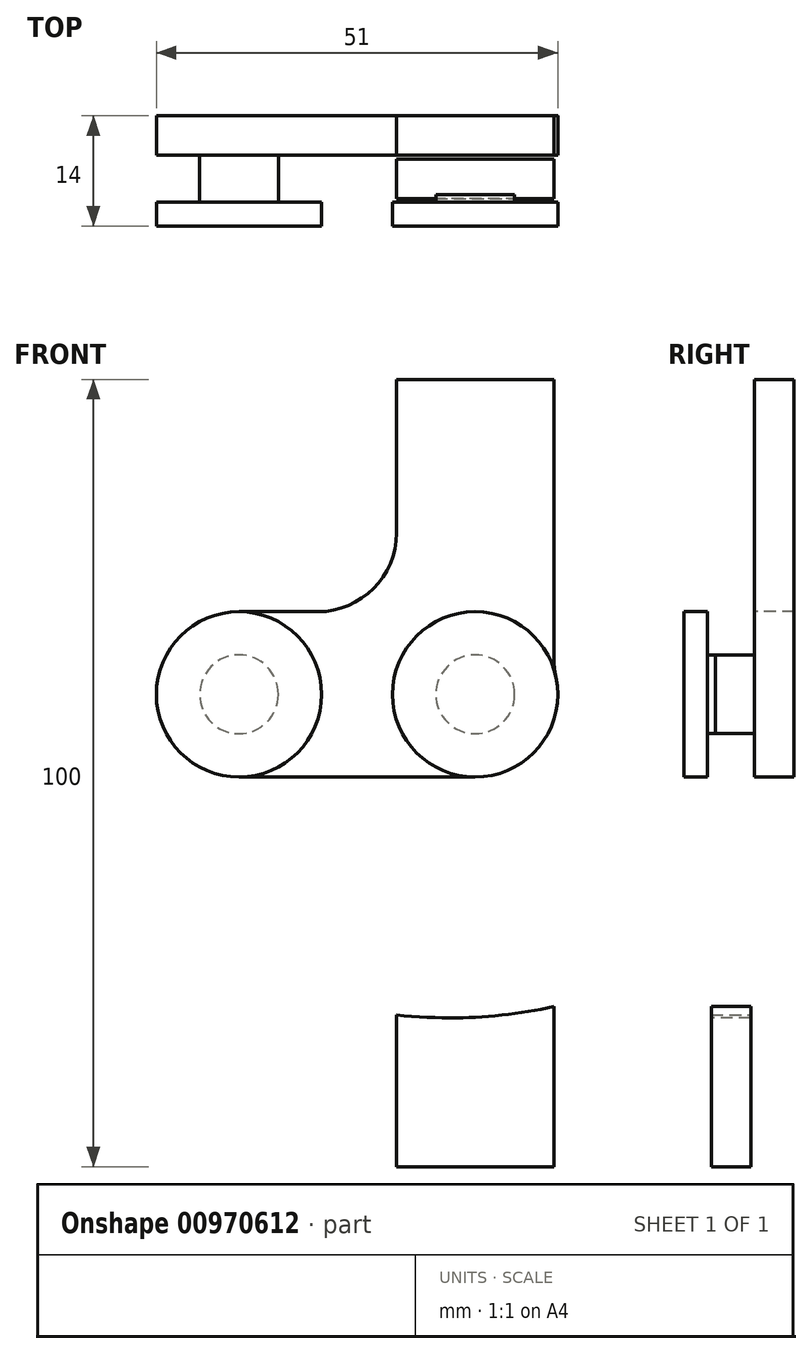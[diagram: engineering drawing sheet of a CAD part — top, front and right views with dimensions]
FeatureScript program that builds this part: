
annotation { "Feature Type Name" : "Feature", "Feature Type Description" : "" }
export const myFeature = defineFeature(function(context is Context, id is Id, definition is map)
    precondition{}
    {
        {
            assignVariable(context, id + "F0", {"name" : "Tbrace", "anyValue" : 5});
        }
        {
            assignVariable(context, id + "F1", {"name" : "Zclearance", "anyValue" : 0.5});
        }
        {
            assignVariable(context, id + "F2", {"name" : "Hpin", "anyValue" : getVariable(context, 'Tbrace') + 2 * getVariable(context, 'Zclearance')});
        }
        {
            assignVariable(context, id + "F3", {"name" : "Tcap", "anyValue" : 3});
        }
        {
            var Q0;
            Q0=qCreatedBy(makeId("Front.planeOp"),FACE);
            var sketch = newSketch(context, id + "F4", { "sketchPlane" : qUnion([Q0])});
            skCircle(sketch, "E0", {"center": v(0, 0) * mm, "radius": 5 * mm});
            skCircle(sketch, "E1", {"center": v(-30, 0) * mm, "radius": 5 * mm});
            skLineSegment(sketch, "E2", {"start": v(0, 0) * mm, "end": v(-30, 0) * mm, "construction": true});
            skSolve(sketch);
        }
        {
            var Q0;
            Q0=qCreatedBy(makeId("Front.planeOp"),FACE);
            var sketch = newSketch(context, id + "F5", { "sketchPlane" : qUnion([Q0])});
            skArc(sketch, "E3", {"start": v(0, 0) * mm, "mid": v(4.76, 8.78) * mm, "end": v(7.87, 18.27) * mm, "construction": true});
            skLineSegment(sketch, "E4", {"start": v(-46.2, 30.74) * mm, "end": v(0, 0) * mm, "construction": true});
            skLineSegment(sketch, "E5", {"start": v(-46.2, 30.74) * mm, "end": v(7.87, 18.27) * mm, "construction": true});
            skArc(sketch, "E6.0.startCap", {"start": v(4.58, -3.05) * mm, "mid": v(-3.05, -4.58) * mm, "end": v(-4.58, 3.05) * mm});
            skArc(sketch, "E6.0.endCap", {"start": v(2.51, 19.5) * mm, "mid": v(9.11, 23.63) * mm, "end": v(13.23, 17.03) * mm});
            skArc(sketch, "E6.0.left", {"start": v(-4.58, 3.05) * mm, "mid": v(-0.29, 10.96) * mm, "end": v(2.51, 19.5) * mm});
            skArc(sketch, "E6.0.right", {"start": v(4.58, -3.05) * mm, "mid": v(9.81, 6.6) * mm, "end": v(13.23, 17.03) * mm});
            skPoint(sketch, "E7", {"position": v(25.08, -6.3) * mm});
            skLineSegment(sketch, "E8", {"start": v(7.87, 18.27) * mm, "end": v(25.08, -6.3) * mm, "construction": true});
            skLineSegment(sketch, "E9.1.0", {"start": v(-46.2, 30.74) * mm, "end": v(1.08, 1.68) * mm, "construction": true});
            skLineSegment(sketch, "E9.2.0", {"start": v(-46.2, 30.74) * mm, "end": v(2.1, 3.4) * mm, "construction": true});
            skLineSegment(sketch, "E9.3.0", {"start": v(-46.2, 30.74) * mm, "end": v(3.05, 5.17) * mm, "construction": true});
            skLineSegment(sketch, "E9.4.0", {"start": v(-46.2, 30.74) * mm, "end": v(3.94, 6.96) * mm, "construction": true});
            skLineSegment(sketch, "E9.5.0", {"start": v(-46.2, 30.74) * mm, "end": v(4.76, 8.78) * mm, "construction": true});
            skLineSegment(sketch, "E9.6.0", {"start": v(-46.2, 30.74) * mm, "end": v(5.52, 10.63) * mm, "construction": true});
            skLineSegment(sketch, "E9.7.0", {"start": v(-46.2, 30.74) * mm, "end": v(6.21, 12.5) * mm, "construction": true});
            skLineSegment(sketch, "E9.8.0", {"start": v(-46.2, 30.74) * mm, "end": v(6.84, 14.4) * mm, "construction": true});
            skLineSegment(sketch, "E9.9.0", {"start": v(-46.2, 30.74) * mm, "end": v(7.39, 16.33) * mm, "construction": true});
            skLineSegment(sketch, "E10", {"start": v(7.39, 16.33) * mm, "end": v(18.87, -11.39) * mm, "construction": true});
            skLineSegment(sketch, "E11", {"start": v(6.84, 14.4) * mm, "end": v(12.04, -15.14) * mm, "construction": true});
            skLineSegment(sketch, "E12", {"start": v(6.21, 12.5) * mm, "end": v(4.9, -17.47) * mm, "construction": true});
            skLineSegment(sketch, "E13", {"start": v(5.52, 10.63) * mm, "end": v(-2.24, -18.35) * mm, "construction": true});
            skLineSegment(sketch, "E14", {"start": v(4.76, 8.78) * mm, "end": v(-9.1, -17.83) * mm, "construction": true});
            skLineSegment(sketch, "E15", {"start": v(3.94, 6.96) * mm, "end": v(-15.35, -16.02) * mm, "construction": true});
            skLineSegment(sketch, "E16", {"start": v(3.05, 5.17) * mm, "end": v(-20.75, -13.1) * mm, "construction": true});
            skLineSegment(sketch, "E17", {"start": v(2.1, 3.4) * mm, "end": v(-25.1, -9.27) * mm, "construction": true});
            skLineSegment(sketch, "E18", {"start": v(1.08, 1.68) * mm, "end": v(-28.21, -4.8) * mm, "construction": true});
            skLineSegment(sketch, "E19", {"start": v(0, 0) * mm, "end": v(-30, 0) * mm, "construction": true});
            skFitSpline(sketch, "E20", {"points": [v(-30, 0) * mm, v(-28.21, -4.8) * mm, v(-25.1, -9.27) * mm, v(-20.75, -13.1) * mm, v(-15.35, -16.02) * mm, v(-9.1, -17.83) * mm, v(-2.24, -18.35) * mm, v(4.9, -17.47) * mm, v(12.04, -15.14) * mm, v(18.87, -11.39) * mm, v(25.08, -6.3) * mm], "startDerivative": vector(0, -79.8) * mm, "endDerivative": vector(58.42, 58.42) * mm, "construction": true});
            skLineSegment(sketch, "E21.0.startCap", {"start": v(-35.5, 0) * mm, "end": v(-35.5, 0) * mm});
            skLineSegment(sketch, "E21.0.endCap", {"start": v(28.97, -10.2) * mm, "end": v(28.97, -10.2) * mm});
            skFitSpline(sketch, "E21.0.left", {"points": [v(-48, 0) * mm, v(-48, -0.78) * mm, v(-47.9, -2.28) * mm, v(-47.5, -4.33) * mm, v(-46.97, -6.18) * mm, v(-46.46, -7.56) * mm, v(-46.03, -8.58) * mm, v(-45.71, -9.3) * mm, v(-45.45, -9.88) * mm, v(-45.24, -10.32) * mm, v(-45.04, -10.74) * mm, v(-44.78, -11.28) * mm, v(-44.34, -12.15) * mm, v(-43.77, -13.24) * mm, v(-43.02, -14.57) * mm, v(-42.22, -15.9) * mm, v(-41.49, -17) * mm, v(-40.86, -17.88) * mm, v(-40.21, -18.76) * mm, v(-39.37, -19.83) * mm, v(-38.3, -21.06) * mm, v(-37.19, -22.25) * mm, v(-35.65, -23.76) * mm, v(-33.63, -25.52) * mm, v(-30.22, -28.1) * mm, v(-26.52, -30.33) * mm, v(-22.58, -32.16) * mm, v(-18.53, -33.72) * mm, v(-13.25, -35.16) * mm, v(-6.74, -36.05) * mm, v(-1.22, -36.1) * mm, v(3.19, -35.74) * mm, v(7.6, -35.1) * mm, v(11.94, -34.06) * mm, v(16.16, -32.67) * mm, v(19.25, -31.44) * mm, v(22.28, -30.04) * mm, v(24.76, -28.7) * mm, v(26.73, -27.55) * mm, v(28.69, -26.32) * mm, v(31.12, -24.67) * mm, v(33.92, -22.52) * mm, v(35.65, -20.98) * mm, v(36.47, -20.15) * mm]});
            skFitSpline(sketch, "E21.0.right", {"points": [v(-48, 0) * mm, v(-48, -0.78) * mm, v(-47.9, -2.28) * mm, v(-47.5, -4.33) * mm, v(-46.97, -6.18) * mm, v(-46.46, -7.56) * mm, v(-46.03, -8.58) * mm, v(-45.71, -9.3) * mm, v(-45.45, -9.88) * mm, v(-45.24, -10.32) * mm, v(-45.04, -10.74) * mm, v(-44.78, -11.28) * mm, v(-44.34, -12.15) * mm, v(-43.77, -13.24) * mm, v(-43.02, -14.57) * mm, v(-42.22, -15.9) * mm, v(-41.49, -17) * mm, v(-40.86, -17.88) * mm, v(-40.21, -18.76) * mm, v(-39.37, -19.83) * mm, v(-38.3, -21.06) * mm, v(-37.19, -22.25) * mm, v(-35.65, -23.76) * mm, v(-33.63, -25.52) * mm, v(-30.22, -28.1) * mm, v(-26.52, -30.33) * mm, v(-22.58, -32.16) * mm, v(-18.53, -33.72) * mm, v(-13.25, -35.16) * mm, v(-6.74, -36.05) * mm, v(-1.22, -36.1) * mm, v(3.19, -35.74) * mm, v(7.6, -35.1) * mm, v(11.94, -34.06) * mm, v(16.16, -32.67) * mm, v(19.25, -31.44) * mm, v(22.28, -30.04) * mm, v(24.76, -28.7) * mm, v(26.73, -27.55) * mm, v(28.69, -26.32) * mm, v(31.12, -24.67) * mm, v(33.92, -22.52) * mm, v(35.65, -20.98) * mm, v(36.47, -20.15) * mm]});
            skFitSpline(sketch, "E22.0", {"points": [v(-32, 0) * mm, v(-32, -0.05) * mm, v(-32, -0.17) * mm, v(-31.96, -0.4) * mm, v(-31.92, -0.6) * mm, v(-31.85, -0.86) * mm, v(-31.76, -1.16) * mm, v(-31.64, -1.5) * mm, v(-31.5, -1.86) * mm, v(-31.33, -2.27) * mm, v(-31.14, -2.7) * mm, v(-30.92, -3.18) * mm, v(-30.68, -3.69) * mm, v(-30.43, -4.19) * mm, v(-30.1, -4.83) * mm, v(-29.7, -5.62) * mm, v(-29.2, -6.5) * mm, v(-28.69, -7.35) * mm, v(-28.16, -8.14) * mm, v(-27.63, -8.89) * mm, v(-27.05, -9.61) * mm, v(-26.42, -10.34) * mm, v(-25.75, -11.05) * mm, v(-25.04, -11.75) * mm, v(-24.3, -12.43) * mm, v(-23.51, -13.1) * mm, v(-22.7, -13.73) * mm, v(-21.58, -14.54) * mm, v(-20.41, -15.3) * mm, v(-19.2, -16) * mm, v(-17.95, -16.67) * mm, v(-16.33, -17.42) * mm, v(-13.64, -18.46) * mm, v(-10.78, -19.24) * mm, v(-7.83, -19.74) * mm, v(-4.8, -20.06) * mm, v(-1.72, -20.09) * mm, v(1.38, -19.83) * mm, v(3.72, -19.5) * mm, v(6.07, -19) * mm, v(8.4, -18.38) * mm, v(10.7, -17.62) * mm, v(12.92, -16.74) * mm, v(14.75, -15.9) * mm, v(16.2, -15.13) * mm, v(17.31, -14.52) * mm, v(18.43, -13.87) * mm, v(19.56, -13.16) * mm, v(20.67, -12.43) * mm, v(21.75, -11.67) * mm, v(22.6, -11.04) * mm, v(23.23, -10.55) * mm, v(23.68, -10.18) * mm, v(24.1, -9.82) * mm, v(24.62, -9.36) * mm, v(24.96, -9.04) * mm, v(25.16, -8.84) * mm]});
            skArc(sketch, "E23", {"start": v(-35.5, 0) * mm, "mid": v(-30, 5.5) * mm, "end": v(-24.5, 0) * mm});
            skArc(sketch, "E24", {"start": v(28.97, -10.2) * mm, "mid": v(28.97, -2.42) * mm, "end": v(21.2, -2.42) * mm});
            skLineSegment(sketch, "E25", {"start": v(25.08, -6.3) * mm, "end": v(22.93, -8.45) * mm, "construction": true});
            skSolve(sketch);
        }
        {
            var Q0;
            Q0=qCreatedBy(makeId("Front.planeOp"),FACE);
            var sketch = newSketch(context, id + "F6", { "sketchPlane" : qUnion([Q0])});
            skArc(sketch, "E26", {"start": v(-30, 10.5) * mm, "mid": v(-40.5, 0) * mm, "end": v(-30, -10.5) * mm});
            skArc(sketch, "E27", {"start": v(0, -10.5) * mm, "mid": v(8.2, -6.56) * mm, "end": v(10.24, 2.3) * mm});
            skLineSegment(sketch, "E28", {"start": v(-30, -10.5) * mm, "end": v(0, -10.5) * mm});
            skLineSegment(sketch, "E29", {"start": v(-30, 10.5) * mm, "end": v(-20, 10.5) * mm});
            skLineSegment(sketch, "E30", {"start": v(-10, 20.5) * mm, "end": v(-10, 40) * mm});
            skLineSegment(sketch, "E31", {"start": v(10, 4.5) * mm, "end": v(10, 40) * mm});
            skLineSegment(sketch, "E32", {"start": v(10, 40) * mm, "end": v(-10, 40) * mm});
            skPoint(sketch, "E33", {"position": v(0, 40) * mm});
            skPoint(sketch, "E34.visualSharp", {"position": v(10, 3.2) * mm});
            skArc(sketch, "E34.filletArc", {"start": v(10, 4.5) * mm, "mid": v(10.06, 3.4) * mm, "end": v(10.24, 2.3) * mm});
            skPoint(sketch, "E35.visualSharp", {"position": v(-10, 10.5) * mm});
            skArc(sketch, "E35.filletArc", {"start": v(-20, 10.5) * mm, "mid": v(-12.93, 13.43) * mm, "end": v(-10, 20.5) * mm});
            skSolve(sketch);
        }
        {
            var Q0;
            Q0=qCreatedBy(makeId("Front.planeOp"),FACE);
            var sketch = newSketch(context, id + "F7", { "sketchPlane" : qUnion([Q0])});
            skArc(sketch, "E36", {"start": v(-34.56, 9.46) * mm, "mid": v(-38.9, 5.58) * mm, "end": v(-40.5, 0) * mm});
            skArc(sketch, "E37", {"start": v(32.5, -13.73) * mm, "mid": v(35.54, -7.22) * mm, "end": v(33.68, -0.28) * mm});
            skArc(sketch, "E38", {"start": v(16.47, 24.3) * mm, "mid": v(10.52, 28.43) * mm, "end": v(3.31, 27.73) * mm});
            skFitSpline(sketch, "E39.0", {"points": [v(-53, 0) * mm, v(-53, -1) * mm, v(-52.86, -2.92) * mm, v(-52.38, -5.5) * mm, v(-51.72, -7.76) * mm, v(-51.12, -9.39) * mm, v(-50.63, -10.56) * mm, v(-50.27, -11.37) * mm, v(-49.98, -12) * mm, v(-49.76, -12.47) * mm, v(-49.54, -12.92) * mm, v(-49.26, -13.5) * mm, v(-48.79, -14.44) * mm, v(-48.16, -15.63) * mm, v(-47.34, -17.08) * mm, v(-46.45, -18.57) * mm, v(-45.62, -19.81) * mm, v(-44.92, -20.81) * mm, v(-44.18, -21.81) * mm, v(-43.22, -23.02) * mm, v(-42.01, -24.42) * mm, v(-40.76, -25.74) * mm, v(-39.47, -27.01) * mm, v(-38.14, -28.22) * mm, v(-36.78, -29.38) * mm, v(-35.37, -30.48) * mm, v(-33.45, -31.88) * mm, v(-30.95, -33.5) * mm, v(-27.8, -35.25) * mm, v(-24.54, -36.77) * mm, v(-21.18, -38.06) * mm, v(-17.74, -39.12) * mm, v(-13.06, -40.23) * mm, v(-8.29, -40.89) * mm, v(-3.48, -41.08) * mm, v(0.14, -41) * mm, v(3.75, -40.71) * mm, v(7.36, -40.19) * mm, v(10.93, -39.45) * mm, v(14.43, -38.5) * mm, v(17.87, -37.37) * mm, v(21.23, -36.04) * mm, v(24.52, -34.5) * mm, v(27.74, -32.78) * mm, v(30.9, -30.87) * mm, v(34.04, -28.73) * mm, v(37.1, -26.39) * mm, v(39.05, -24.65) * mm, v(40, -23.69) * mm]});
            skLineSegment(sketch, "E40", {"start": v(-34.56, 9.46) * mm, "end": v(3.31, 27.73) * mm});
            skLineSegment(sketch, "E41", {"start": v(16.47, 24.3) * mm, "end": v(33.68, -0.28) * mm});
            skLineSegment(sketch, "E42", {"start": v(-10, -36.15) * mm, "end": v(-10, -60) * mm});
            skLineSegment(sketch, "E43", {"start": v(10, -34.03) * mm, "end": v(10, -60) * mm});
            skLineSegment(sketch, "E44", {"start": v(10, -60) * mm, "end": v(-10, -60) * mm});
            skPoint(sketch, "E45", {"position": v(0, -60) * mm});
            skFitSpline(sketch, "E46.trimOffspring", {"points": [v(-53, 0) * mm, v(-53, -1) * mm, v(-52.86, -2.92) * mm, v(-52.38, -5.5) * mm, v(-51.72, -7.76) * mm, v(-51.12, -9.39) * mm, v(-50.63, -10.56) * mm, v(-50.27, -11.37) * mm, v(-49.98, -12) * mm, v(-49.76, -12.47) * mm, v(-49.54, -12.92) * mm, v(-49.26, -13.5) * mm, v(-48.79, -14.44) * mm, v(-48.16, -15.63) * mm, v(-47.34, -17.08) * mm, v(-46.45, -18.57) * mm, v(-45.62, -19.81) * mm, v(-44.92, -20.81) * mm, v(-44.18, -21.81) * mm, v(-43.22, -23.02) * mm, v(-42.01, -24.42) * mm, v(-40.76, -25.74) * mm, v(-39.47, -27.01) * mm, v(-38.14, -28.22) * mm, v(-36.78, -29.38) * mm, v(-35.37, -30.48) * mm, v(-33.45, -31.88) * mm, v(-30.95, -33.5) * mm, v(-27.8, -35.25) * mm, v(-24.54, -36.77) * mm, v(-21.18, -38.06) * mm, v(-17.74, -39.12) * mm, v(-13.06, -40.23) * mm, v(-8.29, -40.89) * mm, v(-3.48, -41.08) * mm, v(0.14, -41) * mm, v(3.75, -40.71) * mm, v(7.36, -40.19) * mm, v(10.93, -39.45) * mm, v(14.43, -38.5) * mm, v(17.87, -37.37) * mm, v(21.23, -36.04) * mm, v(24.52, -34.5) * mm, v(27.74, -32.78) * mm, v(30.9, -30.87) * mm, v(34.04, -28.73) * mm, v(37.1, -26.39) * mm, v(39.05, -24.65) * mm, v(40, -23.69) * mm]});
            skPoint(sketch, "E47.visualSharp", {"position": v(-10, -28.33) * mm});
            skArc(sketch, "E47.filletArc", {"start": v(-10, -36.15) * mm, "mid": v(-11.89, -30.3) * mm, "end": v(-16.83, -26.67) * mm});
            skPoint(sketch, "E48.visualSharp", {"position": v(10, -27) * mm});
            skArc(sketch, "E48.filletArc", {"start": v(16.03, -24.85) * mm, "mid": v(11.64, -28.54) * mm, "end": v(10, -34.03) * mm});
            skSolve(sketch);
        }
        {
            var Q0;
            Q0 = qSketchRegion(id + "F6", true);
            extrude(context, id + "F8", {"entities" : qUnion([Q0]), "oppositeDirection" : true, "depth" : (getVariable(context, 'Tbrace')) * mm, "offsetDistance" : 25 * mm});
        }
        {
            var Q0;
            Q0 = qSketchRegion(id + "F4", true);
            extrude(context, id + "F9", {"entities" : qUnion([Q0]), "operationType" : NewBodyOperationType.ADD, "depth" : (getVariable(context, 'Hpin')) * mm, "offsetDistance" : 25 * mm});
        }
        {
            var Q0;
            Q0 = qSketchRegion(id + "F7", true);
            extrude(context, id + "F10", {"entities" : qUnion([Q0]), "depth" : (getVariable(context, 'Tbrace')) * mm, "offsetDistance" : 25 * mm});
        }
        {
            var Q0;
            Q0 = qSketchRegion(id + "F5", true);
            var Q1;
            Q1=makeQuery(id+"F10.opExtrude","CAP_FACE",FACE,{"disambiguationData":[OSD([sQuery(id+"F7.wireOp",EDGE,"E36"),sQuery(id+"F7.wireOp",EDGE,"E37"),sQuery(id+"F7.wireOp",EDGE,"E38"),sQuery(id+"F7.wireOp",EDGE,"E39.0"),sQuery(id+"F7.wireOp",EDGE,"E40"),sQuery(id+"F7.wireOp",EDGE,"E41"),sQuery(id+"F7.wireOp",EDGE,"E42"),sQuery(id+"F7.wireOp",EDGE,"E43"),sQuery(id+"F7.wireOp",EDGE,"E44"),sQuery(id+"F7.wireOp",EDGE,"E46.trimOffspring"),sQuery(id+"F7.wireOp",EDGE,"E47.filletArc"),sQuery(id+"F7.wireOp",EDGE,"E48.filletArc")])],"isStart":false});
            extrude(context, id + "F11", {"entities" : qUnion([Q0]), "operationType" : NewBodyOperationType.REMOVE, "endBound" : BoundingType.UP_TO_SURFACE, "depth" : 25 * mm, "endBoundEntityFace" : qUnion([Q1]), "offsetDistance" : 25 * mm});
        }
        {
            var Q0;
            Q0=makeQuery(id+"F10.opExtrude","SWEPT_BODY",BODY,{"disambiguationData":[OSD([sQuery(id+"F7.wireOp",EDGE,"E36"),sQuery(id+"F7.wireOp",EDGE,"E37"),sQuery(id+"F7.wireOp",EDGE,"E38"),sQuery(id+"F7.wireOp",EDGE,"E39.0"),sQuery(id+"F7.wireOp",EDGE,"E40"),sQuery(id+"F7.wireOp",EDGE,"E41"),sQuery(id+"F7.wireOp",EDGE,"E42"),sQuery(id+"F7.wireOp",EDGE,"E43"),sQuery(id+"F7.wireOp",EDGE,"E44"),sQuery(id+"F7.wireOp",EDGE,"E46.trimOffspring"),sQuery(id+"F7.wireOp",EDGE,"E47.filletArc"),sQuery(id+"F7.wireOp",EDGE,"E48.filletArc")])]});
            transform(context, id + "F12", {"entities" : qUnion([Q0]), "transformType" : TransformType.TRANSLATION_3D, "dx" : 0 * mm, "dy" : (-getVariable(context, 'Zclearance')) * mm, "dz" : 0 * mm, "makeCopy" : false});
        }
        {
            var Q0;
            Q0=makeQuery(id+"F9.opExtrude","CAP_FACE",FACE,{"disambiguationData":[OSD([sQuery(id+"F4.wireOp",EDGE,"E0")])],"isStart":false});
            var sketch = newSketch(context, id + "F13", { "sketchPlane" : qUnion([Q0])});
            skCircle(sketch, "E49", {"center": v(0, 0) * mm, "radius": 10.5 * mm});
            skCircle(sketch, "E50", {"center": v(-30, 0) * mm, "radius": 10.5 * mm});
            skSolve(sketch);
        }
        {
            var Q0;
            Q0 = qSketchRegion(id + "F13", true);
            extrude(context, id + "F14", {"entities" : qUnion([Q0]), "operationType" : NewBodyOperationType.ADD, "depth" : (getVariable(context, 'Tcap')) * mm, "offsetDistance" : 25 * mm});
        }
    });
